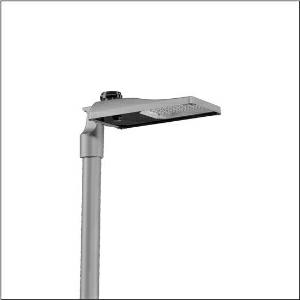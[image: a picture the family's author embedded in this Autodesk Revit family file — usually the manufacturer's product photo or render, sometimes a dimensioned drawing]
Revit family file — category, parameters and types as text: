
# Revit family: streetlight_sl_31_mini___st1_0a_5xh6d3bm08ha_d052
name_source: partatom
category: Lighting Fixtures
units: mm (PartAtom-declared; Revit-internal decimal feet)

## family parameters
Cut with Voids When Loaded = No
Host = Face
Light Source = No
Part Type = Normal
Room Calculation Point = No
Round Connector Dimension = Use Diameter
Shared = No

## types (1)
- --- (1 x LED, 9230 lm, 68.3 W, 3000K)
    Apparent Load = 68 VA
    CIE Flux Codes = 37 72 97 100 100
    Color Rendering = 70
    Color Temperature = 3000K
    Default Elevation = 1800 mm
    Description = Streetlight SL 31 mini NEMA (7pin) mast luminaire for post-top, side-entry; light control with lens of PMMA; light distribution: ST1.0a, direct asymmetric distribution, for standard-compliant lighting for roads and squares; LED: luminous flux: 9.230lm, light colour: 730, colour temperature: 3000K; luminous efficacy: 135,1lm/W; control: pre-setting: linear dimming characteristic, flexible luminous flux parameterisation, time-dependent luminous flux control, constant luminous flux control, intelligent temperature release in ECG and LED module, overheat protection; luminaire housing, of diecast aluminium, SITECO metallic grey (DB 702S), corrosivity category C5 high according to DIN EN ISO 12944; cover of toughened safety glass, transparent, opened without tools; mast flange of diecast aluminium, SITECO metallic grey (DB 702S), spigot size: 76/60mm, mast flange included unmounted; cable length: 8,5m, connection cable pre-assembled; mains connection: 220..240V, AC, 50/60Hz; power consumption (at start of service life): 68,3W / (at end of service life): 74,5W / (with reduced operation 50%): 29,5W; protection rating (complete): IP66; insulation class (complete): insulation class I (protective earthing); impact resistance: IK09; certification: CE, ENEC, ENEC+, VDE, UKCA; permissible operating ambient temperature for outdoor applications: -40..+50°C; packaging unit: 1 piece

Light Distribution: ST1.0a
    Height = 76 mm
    Lamp = 1 x LED
    Lamp Light Flux = 9230 lm
    Lamp Power = 68.3 W
    Lamp count = 1
    Length = 547 mm
    Luminous efficacy = 135 lm/W
    Manufacturer = Siteco
    ModVariant = No
    Model = 5XH6D3BM08HA
    Number of Poles = 1
    OnlyDefault = Yes
    Power Factor = 1
    Product Name = Streetlight SL 31 mini | ST1.0a
    Product group = mast luminaire | pylon top
    ProductGroupID = 6100
    Protection Class = Protection class I
    Protection Degree = IP 66
    RLX_Detail_Level = 1
    RLX_Emergency_Light_Flux = 0 lm
    RLX_Emergency_Type = 0
    RLX_Emergency_Type_DB = No
    RlxData = <blob elided: 24765 chars, md5=a198acce>
    Socket = socket
    Standby Power = 0 W
    System Light Flux = 9230 lm
    System Power = 68 W
    Type Comments = factory setting: luminous flux: 100 % | dim-lin: 254 | 692 mA
    Type Image = l_1300324.jpg
    URL = http://relux.com
    VarID = @adj_020169
    Voltage = 0 V
    Weight = 0.00 kg
    Width = 265 mm

## geometry (parser evidence)
native form markers: Blend x4, Sweep x11
no freeform markers — native parametric forms only
